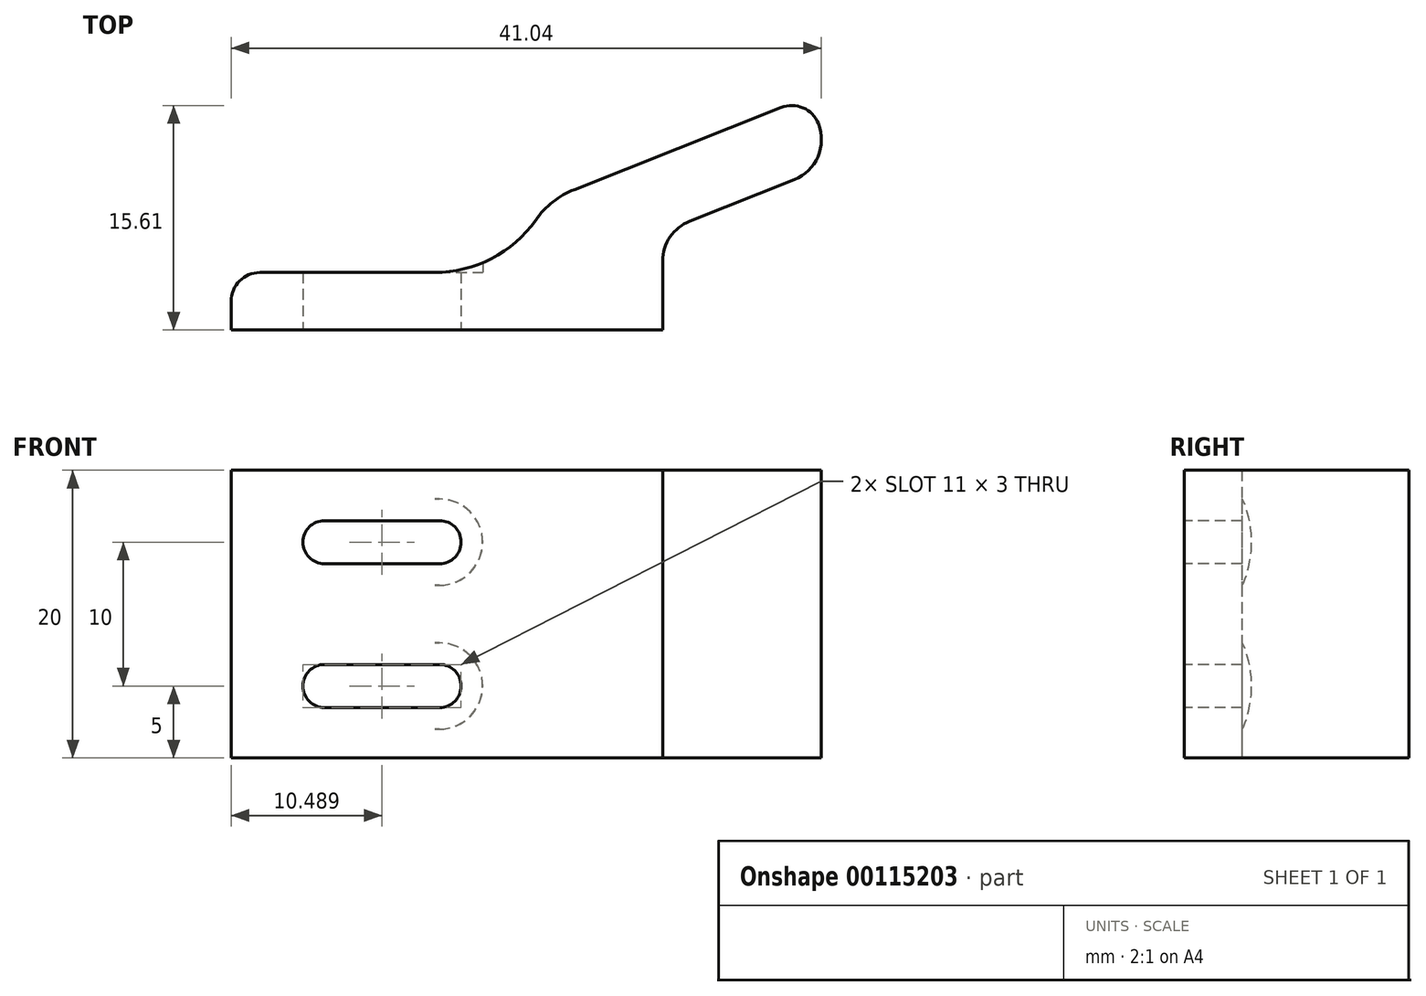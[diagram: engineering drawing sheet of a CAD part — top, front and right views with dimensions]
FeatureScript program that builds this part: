
annotation { "Feature Type Name" : "Feature", "Feature Type Description" : "" }
export const myFeature = defineFeature(function(context is Context, id is Id, definition is map)
    precondition{}
    {
        {
            var Q0;
            Q0=qCreatedBy(makeId("Top.planeOp"),FACE);
            var sketch = newSketch(context, id + "F0", { "sketchPlane" : qUnion([Q0])});
            skLineSegment(sketch, "E0", {"start": v(0, 0) * mm, "end": v(-45, 0) * mm, "construction": true});
            skLineSegment(sketch, "E1", {"start": v(-8, 0) * mm, "end": v(-8, 6.5) * mm, "construction": true});
            skLineSegment(sketch, "E2", {"start": v(-8, 6.5) * mm, "end": v(0, 11.2) * mm, "construction": true});
            skLineSegment(sketch, "E3", {"start": v(0, 26.2) * mm, "end": v(0, -18) * mm, "construction": true});
            skLineSegment(sketch, "E4", {"start": v(-45, 0) * mm, "end": v(-45, -18) * mm, "construction": true});
            skLineSegment(sketch, "E5", {"start": v(-45, -18) * mm, "end": v(0, -18) * mm, "construction": true});
            skSolve(sketch);
        }
        {
            var Q0;
            Q0=qCreatedBy(makeId("Top.planeOp"),FACE);
            var sketch = newSketch(context, id + "F1", { "sketchPlane" : qUnion([Q0])});
            skLineSegment(sketch, "E6", {"start": v(-41.04, 0) * mm, "end": v(-11.04, 0) * mm});
            skLineSegment(sketch, "E7", {"start": v(-11.04, 0) * mm, "end": v(-11.04, 4.79) * mm});
            skLineSegment(sketch, "E8", {"start": v(-9.14, 7.58) * mm, "end": v(-1.9, 10.45) * mm});
            skLineSegment(sketch, "E9.0", {"start": v(-17.17, 9.77) * mm, "end": v(-2.8, 15.47) * mm});
            skLineSegment(sketch, "E10", {"start": v(-0.21, 14.35) * mm, "end": v(-0.21, 14.35) * mm});
            skPoint(sketch, "E11.visualSharp", {"position": v(-11.04, 6.82) * mm});
            skArc(sketch, "E11.filletArc", {"start": v(-9.14, 7.58) * mm, "mid": v(-10.52, 6.47) * mm, "end": v(-11.04, 4.79) * mm});
            skPoint(sketch, "E12.visualSharp", {"position": v(-0.95, 16.2) * mm});
            skArc(sketch, "E12.filletArc", {"start": v(-0.21, 14.35) * mm, "mid": v(-1.28, 15.44) * mm, "end": v(-2.8, 15.47) * mm});
            skPoint(sketch, "E13.visualSharp", {"position": v(0.9, 11.56) * mm});
            skArc(sketch, "E13.filletArc", {"start": v(-1.9, 10.45) * mm, "mid": v(-0.25, 12.05) * mm, "end": v(-0.21, 14.35) * mm});
            skLineSegment(sketch, "E14", {"start": v(-26.88, 4) * mm, "end": v(-39.04, 4) * mm});
            skLineSegment(sketch, "E15", {"start": v(-41.04, 2) * mm, "end": v(-41.04, 0) * mm});
            skPoint(sketch, "E16.visualSharp", {"position": v(-41.04, 4) * mm});
            skArc(sketch, "E16.filletArc", {"start": v(-39.04, 4) * mm, "mid": v(-40.45, 3.41) * mm, "end": v(-41.04, 2) * mm});
            skPoint(sketch, "E17.visualSharp", {"position": v(-12.37, 11.67) * mm});
            skArc(sketch, "E17.filletArc", {"start": v(-17.17, 9.77) * mm, "mid": v(-18.67, 8.9) * mm, "end": v(-19.87, 7.64) * mm});
            skPoint(sketch, "E18.visualSharp", {"position": v(-13.19, 4) * mm});
            skArc(sketch, "E18.filletArc", {"start": v(-26.88, 4) * mm, "mid": v(-22.93, 4.97) * mm, "end": v(-19.87, 7.64) * mm});
            skSolve(sketch);
        }
        {
            var Q0;
            Q0=makeQuery(id+"F1.imprint","IMPRINT",FACE,{"disambiguationData":[TD([[makeQuery(id+"F1.imprint","IMPRINT",EDGE,{"derivedFrom":sQuery(id+"F1.wireOp",EDGE,"E6")}),1.0]])]});
            extrude(context, id + "F2", {"entities" : qUnion([Q0]), "endBound" : BoundingType.SYMMETRIC, "depth" : 20 * mm});
        }
        {
            var Q0;
            Q0=qCreatedBy(makeId("Front.planeOp"),FACE);
            var sketch = newSketch(context, id + "F3", { "sketchPlane" : qUnion([Q0])});
            skLineSegment(sketch, "E19.bottom", {"start": v(-34.55, 5) * mm, "end": v(-26.55, 5) * mm, "construction": true});
            skLineSegment(sketch, "E19.top", {"start": v(-34.55, -5) * mm, "end": v(-26.55, -5) * mm, "construction": true});
            skLineSegment(sketch, "E19.left", {"start": v(-34.55, 5) * mm, "end": v(-34.55, -5) * mm, "construction": true});
            skLineSegment(sketch, "E19.right", {"start": v(-26.55, 5) * mm, "end": v(-26.55, -5) * mm, "construction": true});
            skPoint(sketch, "E19.middle", {"position": v(-30.55, 0) * mm});
            skLineSegment(sketch, "E20", {"start": v(-30.55, 0) * mm, "end": v(-30.55, 10) * mm, "construction": true});
            skPoint(sketch, "E21", {"position": v(-30.55, 5) * mm});
            skArc(sketch, "E22.0.startCap", {"start": v(-34.55, 3.5) * mm, "mid": v(-36.05, 5) * mm, "end": v(-34.55, 6.5) * mm});
            skArc(sketch, "E22.0.endCap", {"start": v(-26.55, 6.5) * mm, "mid": v(-25.05, 5) * mm, "end": v(-26.55, 3.5) * mm});
            skLineSegment(sketch, "E22.0.left", {"start": v(-34.55, 6.5) * mm, "end": v(-26.55, 6.5) * mm});
            skLineSegment(sketch, "E22.0.right", {"start": v(-34.55, 3.5) * mm, "end": v(-26.55, 3.5) * mm});
            skArc(sketch, "E22.1.startCap", {"start": v(-34.55, -6.5) * mm, "mid": v(-36.05, -5) * mm, "end": v(-34.55, -3.5) * mm});
            skArc(sketch, "E22.1.endCap", {"start": v(-26.55, -3.5) * mm, "mid": v(-25.05, -5) * mm, "end": v(-26.55, -6.5) * mm});
            skLineSegment(sketch, "E22.1.left", {"start": v(-34.55, -3.5) * mm, "end": v(-26.55, -3.5) * mm});
            skLineSegment(sketch, "E22.1.right", {"start": v(-34.55, -6.5) * mm, "end": v(-26.55, -6.5) * mm});
            skSolve(sketch);
        }
        {
            var Q0;
            Q0 = qSketchRegion(id + "F3", true);
            extrude(context, id + "F4", {"entities" : qUnion([Q0]), "operationType" : NewBodyOperationType.REMOVE, "oppositeDirection" : true, "depth" : 25 * mm});
        }
        {
            var Q0;
            Q0=makeQuery(id+"F2.opExtrude","SWEPT_FACE",FACE,{"disambiguationData":[OSD([sQuery(id+"F1.wireOp",EDGE,"E14")])]});
            var sketch = newSketch(context, id + "F5", { "sketchPlane" : qUnion([Q0])});
            skArc(sketch, "E23", {"start": v(26.55, -2) * mm, "mid": v(23.55, -5) * mm, "end": v(26.55, -8) * mm});
            skArc(sketch, "E24", {"start": v(26.55, 8) * mm, "mid": v(23.55, 5) * mm, "end": v(26.55, 2) * mm});
            skLineSegment(sketch, "E25", {"start": v(26.55, 8) * mm, "end": v(26.55, 2) * mm, "construction": true});
            skLineSegment(sketch, "E26", {"start": v(26.55, -8) * mm, "end": v(26.55, -2) * mm, "construction": true});
            skLineSegment(sketch, "E27", {"start": v(26.55, 8) * mm, "end": v(30.55, 8) * mm});
            skLineSegment(sketch, "E28", {"start": v(26.55, -2) * mm, "end": v(30.55, -2) * mm});
            skLineSegment(sketch, "E29", {"start": v(26.55, 2) * mm, "end": v(30.55, 2) * mm});
            skLineSegment(sketch, "E30", {"start": v(26.55, -8) * mm, "end": v(30.55, -8) * mm});
            skLineSegment(sketch, "E31", {"start": v(30.55, 8) * mm, "end": v(30.55, 2) * mm});
            skLineSegment(sketch, "E32", {"start": v(30.55, -2) * mm, "end": v(30.55, -8) * mm});
            skSolve(sketch);
        }
        {
            var Q0;
            Q0 = qSketchRegion(id + "F5", true);
            extrude(context, id + "F6", {"entities" : qUnion([Q0]), "operationType" : NewBodyOperationType.REMOVE, "depth" : 25 * mm});
        }
    });
